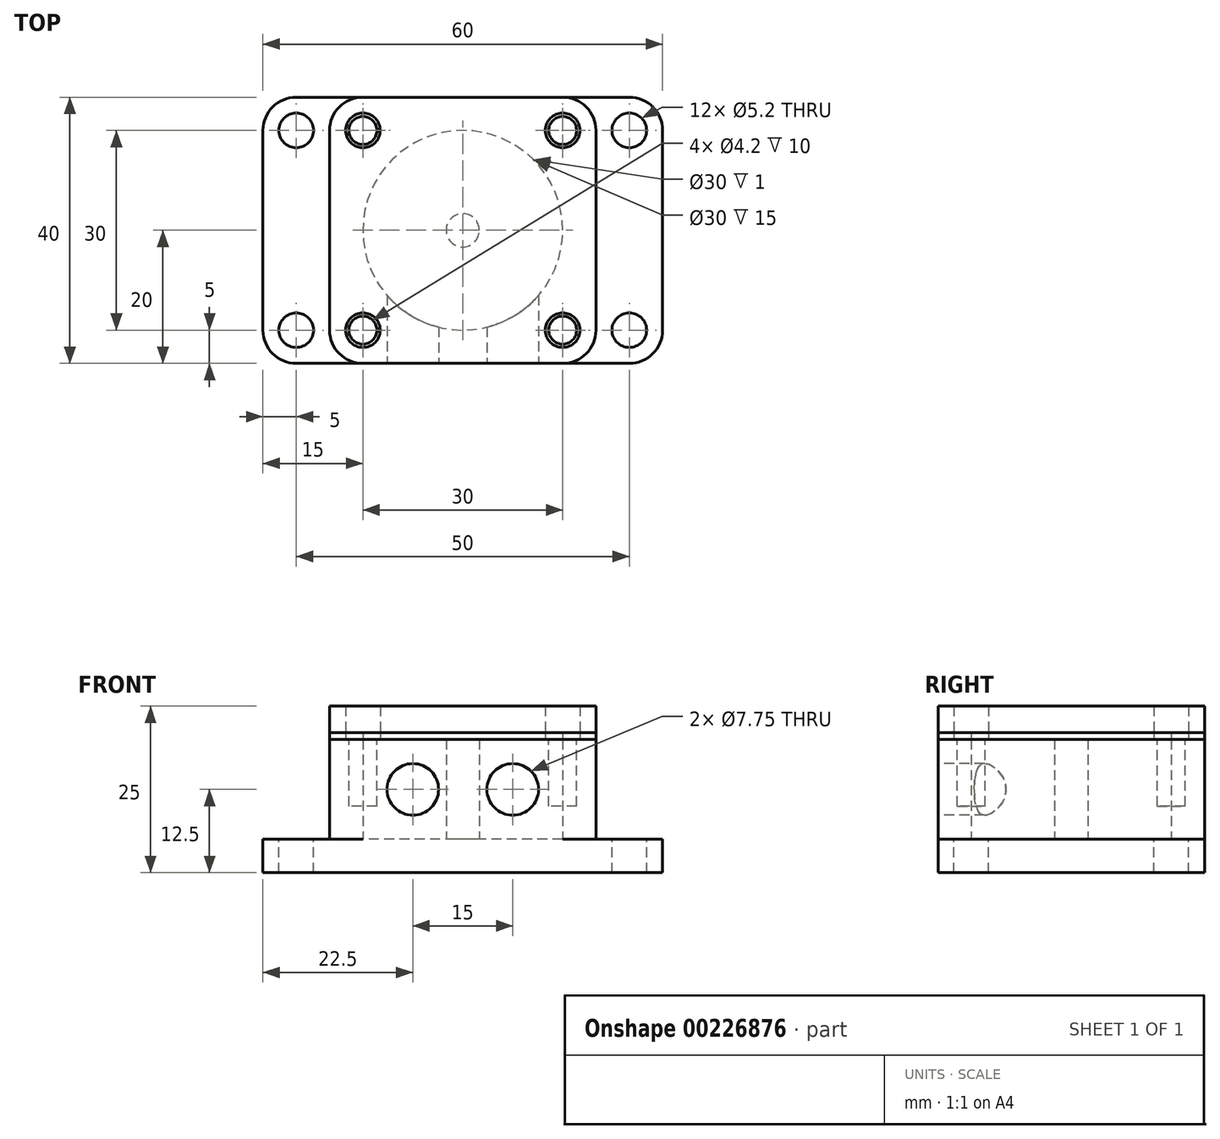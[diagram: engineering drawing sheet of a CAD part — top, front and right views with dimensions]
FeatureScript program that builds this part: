
annotation { "Feature Type Name" : "Feature", "Feature Type Description" : "" }
export const myFeature = defineFeature(function(context is Context, id is Id, definition is map)
    precondition{}
    {
        {
            var Q0;
            Q0=qCreatedBy(makeId("Top.planeOp"),FACE);
            var sketch = newSketch(context, id + "F0", { "sketchPlane" : qUnion([Q0])});
            skLineSegment(sketch, "E0.bottom", {"start": v(30, -20) * mm, "end": v(-30, -20) * mm});
            skLineSegment(sketch, "E0.top", {"start": v(30, 20) * mm, "end": v(-30, 20) * mm});
            skLineSegment(sketch, "E0.left", {"start": v(30, -20) * mm, "end": v(30, 20) * mm});
            skLineSegment(sketch, "E0.right", {"start": v(-30, -20) * mm, "end": v(-30, 20) * mm});
            skPoint(sketch, "E0.middle", {"position": v(0, 0) * mm});
            skSolve(sketch);
        }
        {
            var Q0;
            Q0=makeQuery(id+"F0.imprint","IMPRINT",FACE,{"disambiguationData":[TD([[makeQuery(id+"F0.imprint","IMPRINT",EDGE,{"derivedFrom":sQuery(id+"F0.wireOp",EDGE,"E0.bottom")}),-1.0]])]});
            extrude(context, id + "F1", {"entities" : qUnion([Q0]), "depth" : 5 * mm});
        }
        {
            var Q0;
            Q0=makeQuery(id+"F1.opExtrude","SWEPT_EDGE",EDGE,{"disambiguationData":[OSD([sQuery(id+"F0.wireOp",EDGE,"E0.top"),sQuery(id+"F0.wireOp",EDGE,"E0.right")])]});
            var Q1;
            Q1=makeQuery(id+"F1.opExtrude","SWEPT_EDGE",EDGE,{"disambiguationData":[OSD([sQuery(id+"F0.wireOp",EDGE,"E0.bottom"),sQuery(id+"F0.wireOp",EDGE,"E0.right")])]});
            var Q2;
            Q2=makeQuery(id+"F1.opExtrude","SWEPT_EDGE",EDGE,{"disambiguationData":[OSD([sQuery(id+"F0.wireOp",EDGE,"E0.bottom"),sQuery(id+"F0.wireOp",EDGE,"E0.left")])]});
            var Q3;
            Q3=makeQuery(id+"F1.opExtrude","SWEPT_EDGE",EDGE,{"disambiguationData":[OSD([sQuery(id+"F0.wireOp",EDGE,"E0.top"),sQuery(id+"F0.wireOp",EDGE,"E0.left")])]});
            fillet(context, id + "F2", {"entities" : qUnion([Q0, Q1, Q2, Q3]), "radius" : 5 * mm, "tangentPropagation" : true, "allowEdgeOverflow" : false});
        }
        {
            var Q0;
            Q0=makeQuery(id+"F1.opExtrude","CAP_FACE",FACE,{"disambiguationData":[OSD([sQuery(id+"F0.wireOp",EDGE,"E0.bottom"),sQuery(id+"F0.wireOp",EDGE,"E0.top"),sQuery(id+"F0.wireOp",EDGE,"E0.left"),sQuery(id+"F0.wireOp",EDGE,"E0.right")])],"isStart":false});
            var sketch = newSketch(context, id + "F3", { "sketchPlane" : qUnion([Q0])});
            skLineSegment(sketch, "E1.bottom", {"start": v(20, -20) * mm, "end": v(-20, -20) * mm});
            skLineSegment(sketch, "E1.top", {"start": v(20, 20) * mm, "end": v(-20, 20) * mm});
            skLineSegment(sketch, "E1.left", {"start": v(20, -20) * mm, "end": v(20, 20) * mm});
            skLineSegment(sketch, "E1.right", {"start": v(-20, -20) * mm, "end": v(-20, 20) * mm});
            skPoint(sketch, "E1.middle", {"position": v(0, 0) * mm});
            skCircle(sketch, "E2", {"center": v(0, 0) * mm, "radius": 15 * mm});
            skCircle(sketch, "E3", {"center": v(0, 0) * mm, "radius": 2.5 * mm});
            skSolve(sketch);
        }
        {
            var Q0;
            Q0 = qSketchRegion(id + "F3", true);
            var Q1;
            Q1=makeQuery(id+"F3.imprint","IMPRINT",FACE,{"disambiguationData":[TD([[makeQuery(id+"F3.imprint","IMPRINT",EDGE,{"derivedFrom":sQuery(id+"F3.wireOp",EDGE,"E3")}),1.0]])]});
            extrude(context, id + "F4", {"entities" : qUnion([Q0, Q1]), "operationType" : NewBodyOperationType.ADD, "depth" : 15 * mm});
        }
        {
            var Q0;
            Q0=makeQuery(id+"F4.opExtrude","SWEPT_EDGE",EDGE,{"disambiguationData":[OSD([sQuery(id+"F0.wireOp",EDGE,"E0.top"),sQuery(id+"F3.wireOp",EDGE,"E1.top"),sQuery(id+"F3.wireOp",EDGE,"E1.right")])]});
            var Q1;
            Q1=makeQuery(id+"F4.opExtrude","SWEPT_EDGE",EDGE,{"disambiguationData":[OSD([sQuery(id+"F0.wireOp",EDGE,"E0.bottom"),sQuery(id+"F3.wireOp",EDGE,"E1.bottom"),sQuery(id+"F3.wireOp",EDGE,"E1.right")])]});
            var Q2;
            Q2=makeQuery(id+"F4.opExtrude","SWEPT_EDGE",EDGE,{"disambiguationData":[OSD([sQuery(id+"F0.wireOp",EDGE,"E0.bottom"),sQuery(id+"F3.wireOp",EDGE,"E1.bottom"),sQuery(id+"F3.wireOp",EDGE,"E1.left")])]});
            var Q3;
            Q3=makeQuery(id+"F4.opExtrude","SWEPT_EDGE",EDGE,{"disambiguationData":[OSD([sQuery(id+"F0.wireOp",EDGE,"E0.top"),sQuery(id+"F3.wireOp",EDGE,"E1.top"),sQuery(id+"F3.wireOp",EDGE,"E1.left")])]});
            fillet(context, id + "F5", {"entities" : qUnion([Q0, Q1, Q2, Q3]), "radius" : 5 * mm, "tangentPropagation" : true, "allowEdgeOverflow" : false});
        }
        {
            var Q0;
            {var subQ0=sQuery(id+"F0.wireOp",EDGE,"E0.right");var subQ1=sQuery(id+"F0.wireOp",EDGE,"E0.bottom");var subQ2=sQuery(id+"F0.wireOp",EDGE,"E0.top");Q0=makeQuery(id+"F4.boolean.opBoolean","SPLIT",FACE,{"disambiguationData":[TD([makeQuery(id+"F1.opExtrude","SWEPT_FACE",FACE,{"disambiguationData":[OSD([subQ0])]})])],"derivedFrom":makeQuery(id+"F1.opExtrude","CAP_FACE",FACE,{"disambiguationData":[OSD([subQ1,subQ2,sQuery(id+"F0.wireOp",EDGE,"E0.left"),subQ0])],"isStart":false})});}
            var sketch = newSketch(context, id + "F6", { "sketchPlane" : qUnion([Q0])});
            skCircle(sketch, "E4", {"center": v(-25, 15) * mm, "radius": 2.6 * mm});
            skCircle(sketch, "E5.0.1.0", {"center": v(-25, -15) * mm, "radius": 2.6 * mm});
            skCircle(sketch, "E5.1.0.0", {"center": v(25, 15) * mm, "radius": 2.6 * mm});
            skCircle(sketch, "E5.1.1.0", {"center": v(25, -15) * mm, "radius": 2.6 * mm});
            skLineSegment(sketch, "E5.direction1", {"start": v(-25, 15) * mm, "end": v(25, 15) * mm, "construction": true});
            skLineSegment(sketch, "E5.direction2", {"start": v(-25, 15) * mm, "end": v(-25, -15) * mm, "construction": true});
            skSolve(sketch);
        }
        {
            var Q0;
            Q0 = qSketchRegion(id + "F6", true);
            extrude(context, id + "F7", {"entities" : qUnion([Q0]), "operationType" : NewBodyOperationType.REMOVE, "oppositeDirection" : true, "depth" : 25 * mm});
        }
        {
            var Q0;
            Q0=makeQuery(id+"F4.opExtrude","CAP_FACE",FACE,{"disambiguationData":[OSD([sQuery(id+"F3.wireOp",EDGE,"E1.bottom"),sQuery(id+"F3.wireOp",EDGE,"E1.top"),sQuery(id+"F3.wireOp",EDGE,"E1.left"),sQuery(id+"F3.wireOp",EDGE,"E1.right"),sQuery(id+"F3.wireOp",EDGE,"E2")])],"isStart":false});
            var sketch = newSketch(context, id + "F8", { "sketchPlane" : qUnion([Q0])});
            skLineSegment(sketch, "E6.bottom", {"start": v(15, -15) * mm, "end": v(-15, -15) * mm, "construction": true});
            skLineSegment(sketch, "E6.top", {"start": v(15, 15) * mm, "end": v(-15, 15) * mm, "construction": true});
            skLineSegment(sketch, "E6.left", {"start": v(15, -15) * mm, "end": v(15, 15) * mm, "construction": true});
            skLineSegment(sketch, "E6.right", {"start": v(-15, -15) * mm, "end": v(-15, 15) * mm, "construction": true});
            skPoint(sketch, "E6.middle", {"position": v(0, 0) * mm});
            skCircle(sketch, "E7", {"center": v(-15, 15) * mm, "radius": 2.1 * mm});
            skCircle(sketch, "E8.0.1.0", {"center": v(-15, -15) * mm, "radius": 2.1 * mm});
            skCircle(sketch, "E8.1.0.0", {"center": v(15, 15) * mm, "radius": 2.1 * mm});
            skCircle(sketch, "E8.1.1.0", {"center": v(15, -15) * mm, "radius": 2.1 * mm});
            skLineSegment(sketch, "E8.direction1", {"start": v(-15, 15) * mm, "end": v(15, 15) * mm, "construction": true});
            skLineSegment(sketch, "E8.direction2", {"start": v(-15, 15) * mm, "end": v(-15, -15) * mm, "construction": true});
            skSolve(sketch);
        }
        {
            var Q0;
            Q0 = qSketchRegion(id + "F8", true);
            extrude(context, id + "F9", {"entities" : qUnion([Q0]), "operationType" : NewBodyOperationType.REMOVE, "oppositeDirection" : true, "depth" : 10 * mm});
        }
        {
            var Q0;
            Q0=makeQuery(id+"F4.boolean.opBoolean","MERGE",FACE,{"derivedFrom":[makeQuery(id+"F1.opExtrude","SWEPT_FACE",FACE,{"disambiguationData":[OSD([sQuery(id+"F0.wireOp",EDGE,"E0.bottom")])]}),makeQuery(id+"F4.opExtrude","SWEPT_FACE",FACE,{"disambiguationData":[OSD([sQuery(id+"F3.wireOp",EDGE,"E1.bottom")])]})]});
            var sketch = newSketch(context, id + "F10", { "sketchPlane" : qUnion([Q0])});
            skLineSegment(sketch, "E9", {"start": v(-15, 12.5) * mm, "end": v(15, 12.5) * mm, "construction": true});
            skCircle(sketch, "E10", {"center": v(-7.5, 12.5) * mm, "radius": 3.88 * mm});
            skCircle(sketch, "E11", {"center": v(7.5, 12.5) * mm, "radius": 3.88 * mm});
            skSolve(sketch);
        }
        {
            var Q0;
            Q0 = qSketchRegion(id + "F10", true);
            extrude(context, id + "F11", {"entities" : qUnion([Q0]), "operationType" : NewBodyOperationType.REMOVE, "oppositeDirection" : true, "depth" : 25 * mm});
        }
        {
            var Q0;
            Q0=makeQuery(id+"F4.opExtrude","CAP_FACE",FACE,{"disambiguationData":[OSD([sQuery(id+"F3.wireOp",EDGE,"E1.bottom"),sQuery(id+"F3.wireOp",EDGE,"E1.top"),sQuery(id+"F3.wireOp",EDGE,"E1.left"),sQuery(id+"F3.wireOp",EDGE,"E1.right"),sQuery(id+"F3.wireOp",EDGE,"E2")])],"isStart":false});
            var sketch = newSketch(context, id + "F12", { "sketchPlane" : qUnion([Q0])});
            skLineSegment(sketch, "E12.0.0", {"start": v(15, 20) * mm, "end": v(-15, 20) * mm});
            skArc(sketch, "E12.0.1", {"start": v(-15, 20) * mm, "mid": v(-18.54, 18.54) * mm, "end": v(-20, 15) * mm});
            skLineSegment(sketch, "E12.0.2", {"start": v(-20, 15) * mm, "end": v(-20, -15) * mm});
            skArc(sketch, "E12.0.3", {"start": v(-20, -15) * mm, "mid": v(-18.54, -18.54) * mm, "end": v(-15, -20) * mm});
            skLineSegment(sketch, "E12.0.4", {"start": v(-15, -20) * mm, "end": v(15, -20) * mm});
            skArc(sketch, "E12.0.5", {"start": v(15, -20) * mm, "mid": v(18.54, -18.54) * mm, "end": v(20, -15) * mm});
            skLineSegment(sketch, "E12.0.6", {"start": v(20, -15) * mm, "end": v(20, 15) * mm});
            skArc(sketch, "E12.0.7", {"start": v(20, 15) * mm, "mid": v(18.54, 18.54) * mm, "end": v(15, 20) * mm});
            skCircle(sketch, "E13.0", {"center": v(0, 0) * mm, "radius": 15 * mm});
            skCircle(sketch, "E14", {"center": v(-15, 15) * mm, "radius": 2.6 * mm});
            skCircle(sketch, "E15.0.1.0", {"center": v(-15, -15) * mm, "radius": 2.6 * mm});
            skCircle(sketch, "E15.1.0.0", {"center": v(15, 15) * mm, "radius": 2.6 * mm});
            skCircle(sketch, "E15.1.1.0", {"center": v(15, -15) * mm, "radius": 2.6 * mm});
            skLineSegment(sketch, "E15.direction1", {"start": v(-15, 15) * mm, "end": v(15, 15) * mm, "construction": true});
            skLineSegment(sketch, "E15.direction2", {"start": v(-15, 15) * mm, "end": v(-15, -15) * mm, "construction": true});
            skSolve(sketch);
        }
        {
            var Q0;
            Q0 = qSketchRegion(id + "F12", true);
            extrude(context, id + "F13", {"entities" : qUnion([Q0]), "depth" : 1 * mm});
        }
        {
            var Q0;
            Q0=makeQuery(id+"F13.opExtrude","CAP_FACE",FACE,{"disambiguationData":[OSD([sQuery(id+"F12.wireOp",EDGE,"E12.0.0"),sQuery(id+"F12.wireOp",EDGE,"E12.0.1"),sQuery(id+"F12.wireOp",EDGE,"E12.0.2"),sQuery(id+"F12.wireOp",EDGE,"E12.0.3"),sQuery(id+"F12.wireOp",EDGE,"E12.0.4"),sQuery(id+"F12.wireOp",EDGE,"E12.0.5"),sQuery(id+"F12.wireOp",EDGE,"E12.0.6"),sQuery(id+"F12.wireOp",EDGE,"E12.0.7"),sQuery(id+"F12.wireOp",EDGE,"E13.0"),sQuery(id+"F12.wireOp",EDGE,"E14"),sQuery(id+"F12.wireOp",EDGE,"E15.0.1.0"),sQuery(id+"F12.wireOp",EDGE,"E15.1.0.0"),sQuery(id+"F12.wireOp",EDGE,"E15.1.1.0")])],"isStart":false});
            var sketch = newSketch(context, id + "F14", { "sketchPlane" : qUnion([Q0])});
            skArc(sketch, "E16.0.0", {"start": v(20, 15) * mm, "mid": v(18.54, 18.54) * mm, "end": v(15, 20) * mm});
            skLineSegment(sketch, "E16.0.1", {"start": v(15, 20) * mm, "end": v(-15, 20) * mm});
            skArc(sketch, "E16.0.2", {"start": v(-15, 20) * mm, "mid": v(-18.54, 18.54) * mm, "end": v(-20, 15) * mm});
            skLineSegment(sketch, "E16.0.3", {"start": v(-20, 15) * mm, "end": v(-20, -15) * mm});
            skArc(sketch, "E16.0.4", {"start": v(-20, -15) * mm, "mid": v(-18.54, -18.54) * mm, "end": v(-15, -20) * mm});
            skLineSegment(sketch, "E16.0.5", {"start": v(-15, -20) * mm, "end": v(15, -20) * mm});
            skArc(sketch, "E16.0.6", {"start": v(15, -20) * mm, "mid": v(18.54, -18.54) * mm, "end": v(20, -15) * mm});
            skLineSegment(sketch, "E16.0.7", {"start": v(20, -15) * mm, "end": v(20, 15) * mm});
            skCircle(sketch, "E17.0", {"center": v(15, 15) * mm, "radius": 2.6 * mm});
            skCircle(sketch, "E18.0", {"center": v(-15, 15) * mm, "radius": 2.6 * mm});
            skCircle(sketch, "E19.0", {"center": v(15, -15) * mm, "radius": 2.6 * mm});
            skCircle(sketch, "E20.0", {"center": v(-15, -15) * mm, "radius": 2.6 * mm});
            skSolve(sketch);
        }
        {
            var Q0;
            Q0 = qSketchRegion(id + "F14", true);
            extrude(context, id + "F15", {"entities" : qUnion([Q0]), "depth" : 4 * mm});
        }
    });
